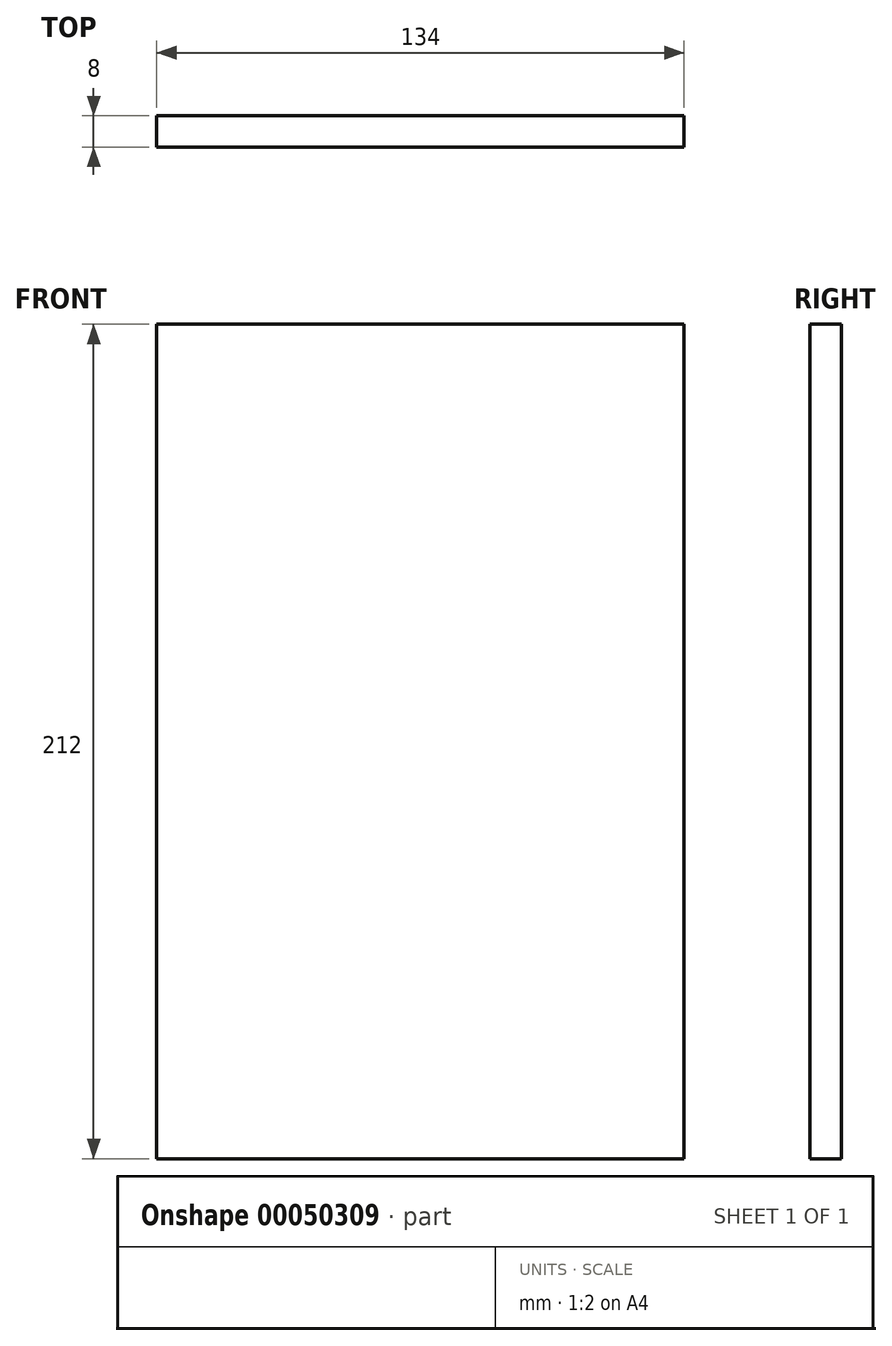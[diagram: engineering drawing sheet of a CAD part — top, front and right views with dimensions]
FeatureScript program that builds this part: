
annotation { "Feature Type Name" : "Feature", "Feature Type Description" : "" }
export const myFeature = defineFeature(function(context is Context, id is Id, definition is map)
    precondition{}
    {
        {
            var Q0;
            Q0=qCreatedBy(makeId("Front.planeOp"),FACE);
            var sketch = newSketch(context, id + "F0", { "sketchPlane" : qUnion([Q0])});
            skLineSegment(sketch, "E0.bottom", {"start": v(0, 0) * mm, "end": v(-134, 0) * mm});
            skLineSegment(sketch, "E0.top", {"start": v(0, -212) * mm, "end": v(-134, -212) * mm});
            skLineSegment(sketch, "E0.left", {"start": v(0, 0) * mm, "end": v(0, -212) * mm});
            skLineSegment(sketch, "E0.right", {"start": v(-134, 0) * mm, "end": v(-134, -212) * mm});
            skSolve(sketch);
        }
        {
            var Q0;
            Q0 = qSketchRegion(id + "F0", true);
            extrude(context, id + "F1", {"entities" : qUnion([Q0]), "depth" : 8 * mm});
        }
    });
